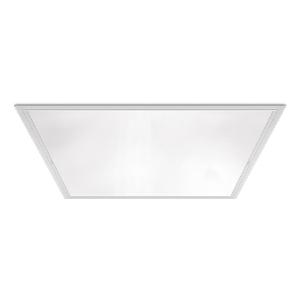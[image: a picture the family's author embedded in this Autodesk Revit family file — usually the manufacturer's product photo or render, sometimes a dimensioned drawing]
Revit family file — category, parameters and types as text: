
# Revit family: 3f_filippi_-_l_600_luce_diffusa_lgs_3f_filippi_-_22825_-_l_600_42w-840_dali_lgs_599x599
name_source: partatom
category: Lighting Fixtures
units: mm (PartAtom-declared; Revit-internal decimal feet)

## family parameters
Cut with Voids When Loaded = No
Host = Face
Light Source = No
Part Type = Normal
Room Calculation Point = No
Round Connector Dimension = Use Diameter
Shared = No

## types (1)
- 3F Filippi - L 600 Luce Diffusa LGS (1 x LED, 5776 lm, 45 W, 4000 K)
    Apparent Load = 45 VA
    Approval mark = ENEC
    CIE Flux Codes = 66 93 98 100 100
    Color Rendering = 80
    Color Temperature = 4000 K
    Control Gear = Electronic transformer
    Default Elevation = 1800 mm
    Description = ILLUMINOTECHNICAL
Luminous efficiency 100% (DLOR 100%, ULOR 0%).
Initial luminous flux of the luminaire 5776 lm.
Direct symmetric distribution.
Installation Interdistance Transv.D = 1.14 x hu - Long.D = 1.16 x hu.
Average luminance <3000 cd/m² for radial angles >65°.
Tabular UGR (CIE 117 - 4H-8H; S=0.25H; 70/50/20): RUG 17.9 - 17.8.
Beam angle: 85° - 85°.
Luminous efficacy 128 lm/W.
Lifetime (L93/B10): 30000 h. (tq+25°C)
Lifetime (L90/B10): 50000 h. (tq+25°C)
Lifetime (L85/B10): 80000 h. (tq+25°C)
Lifetime (L80/B10): 100000 h. (tq+25°C)
Sudden decreased luminous flux after 50000 hours: 0% (C0).
Photobiological safety in compliance with IEC/TR 62778: RG0 risk exempt, (IEC 62471).
In compliance with IEC/EN 62722-2-1 - IEC/EN 62717 standards.

SOURCE
Squared LED module 42W/840.
Source with special protection against aggressive chemically-volatile substances for standard LED technology.
Energy efficiency class (UE 2019/2020 - UE 2019/2015): D.
CIE 13.3 Colour rendering index: CRI >80 (R9 <50%).
IES TM-30 Fidelity Index: Rf = 84 Rg = 95.
CCT nominal colour temperature 4000 K.
Colour initial tolerance (MacAdam): SDCM 3.

MECHANICAL
Housing in galvannealed steel, painted in white epoxy-polyester.
Perimetral frame in white polycarbonate.
LGS micro-prismatic flat diffuser in transparent methacrylate (PMMA), multi-lenticular exterior, anti-glare.
Anti-glare opal polycarbonate filter for brightness uniformity.
Luminaire with limited surface temperature. - D - (EN 60598-2-24)
Dimensions: 599x599 mm, height 95 mm. Weight 5.1 kg.
IP65 protection degree for exposed part, IP64 for recessed part.
Mechanical strength to impacts IK06 (1 joule).
Glow-wire test resistance 650°C.

ELECTRICAL
Halogen Free DALI-2, PUSH-DIM, electronic wiring 230V-50/60Hz, power factor 0.95 at full load, THD <25%, constant output current, class I, 1 driver, 1 DALI addresse.
Power of the luminaire 45 W.
CE - IEC 60598-1 - EN 60598-1.
SAFE FLICKER: PstLM=<1 and SVM=<0.4 (IEC TR 61547-1 and IEC TR 63158), to ensure a more comfortable and safe light.
Luminaire compliant with EN 60598-2-22 for power supply from a centralised emergency system CPSS (Central Power Supply System), not incorporated in the luminaire - high risk areas excluded. The default power and flux are 100% in AC and 15% in DC.
Ambient temperature from 0°C to +40°C.
Temperature class T6 max 85°C.
5-pole terminal block (L-N-PE-DA/DA) quick connection for line connection with connection capacity 2x2.5 mm² per poles.
Relative humidity UR: <85%.

INSTALLATION
Trimless recessed fitting, to be used with inspectable false-ceilings that can be inspected using fixing brackets which are always required, also designed for the hanging from rough ceiling.
All accessories dedicated to this product are available on the Catalog and on our website www.3F-Filippi.com.

APPLICATIONS
Suitable product for food production plants (HACCP), IFS (Food Version 6), BRC (GSFS Food Version 7).
In environments requiring protection and simplified cleaning.
Hospitals, pharmaceutical, chemical, aseptic laboratories, sterilised rooms.
Environments with VDTs.
Environments where demanding visual tasks are performed and soft diffuse light is required for optimal visual comfort and total shielding of the light source.

LIGHT MANAGEMENT
Recommended minimum setting: 10%.
The device, equipped with DALI-2 driver, can be controlled manually with 3F Easy Dim technology or automatically/manually with 3F Smart Dimming technology and/or centralised DALI systems.
DALI-2 certification guarantees interoperability with other devices with the same certification.
In electrical systems without a regulation system (manual or automatic) and DALI bus, a suitable jumper must be made on the DA-DA terminals of the appliance.

WARNING
Luminaire designed for disposal/recycling at end-of-life.
Replaceable (LED only) light source by a professional. Replaceable control gear by a professional.
    Height = 0 mm  [stored 0 ft]
    Lamp = 1 x LED
    Lamp Light Flux = 5776 lm
    Lamp Power = 45 W
    Lamp count = 1
    Length = 599 mm
    Lifetime = 50000 h
    Luminous efficacy = 128 lm/W
    Manufacturer = 3F Filippi
    ModVariant = No
    Model = 3F Filippi - 22825 - L 600 42W-840 DALI LGS 599x599
    Mounting Place = Ceiling
    Mounting Type = Recessed
    Number of Poles = 1
    OnlyDefault = Yes
    Power Factor = 1
    Product Name = 3F Filippi - L 600 Luce Diffusa LGS
    Product group = recessed luminaire
    ProductGroupID = 4
    Protection Class = Protection class I
    Protection Degree = IP 64
    RLX_Detail_Level = 1
    RLX_Emergency_Light_Flux = 0 lm
    RLX_Emergency_Type = 0
    RLX_Emergency_Type_DB = No
    RlxData = <blob elided: 130077 chars, md5=5bd8d6e5>
    Socket = socket
    Standby Power = 0 W
    System Light Flux = 5776 lm
    System Power = 45 W
    Type Comments = Product without accessories
    Type Image = 3ffilippi_l_600_luce_diffusa_lgs.jpg
    URL = http://relux.com
    VarID = ---
    Voltage = 0 V
    Weight = 0.00 kg
    Width = 599 mm

note: [stored X ft] marks values corroborated as IEEE doubles in the binary element streams (Revit-internal decimal feet)

## geometry (parser evidence)
native form markers: Blend x4, Sweep x9
no freeform markers — native parametric forms only
